# Revit family: Faucet_Kitchen-Two_Handle-American_Standard-Monterrey-6500.27X_Series
name_source: partatom
category: Plumbing Fixtures
units: mm (PartAtom-declared; Revit-internal decimal feet)

## family parameters
Always vertical = No
Cut with Voids When Loaded = No
OmniClass Number = 23.45.55.17
OmniClass Title = Mixing Faucets
Part Type = Normal
Room Calculation Point = No
Round Connector Dimension = Use Diameter
Shared = Yes
Work Plane-Based = Yes

## types (2) — shared parameters
ADA Compliant = Yes
ASME A112.18.1/CSA B125.1 = Yes
Assembly Code = D2020300
CW Connection = Yes
CWFU = 1.5
Cold Water Connection Diameter = 1/2"
Cold Water Connection Radius = 1/4"
Default Elevation = 0"
Description = Monterrey Two-Handle 8" Widespread Lavatory Faucet With Conventional Spout and Flexible Underbody.
Finish = Chrome-American_Standard-002-Polished
HW Connection = Yes
HWFU = 1.5
Height = 3 1/4"
Hot Water Connection Diameter = 1"
Hot Water Connection Radius = 1/4"
Installation Type = Deck Mounted
Length = 4 1/16"
Manufacturer = American Standard
Material = Chrome-American_Standard-002-Polished
Price = Prices may vary. Please consult Manufacturer Representative for most up-to-date price list.
Product Documentation Link = https://americanstandard.box.com
Product Page URL = https://www.americanstandard-us.com
URL = https://www.americanstandard-us.com
Vent Connection = No
WFU = 2
Waste Connection = No

## per-type parameters (varying)
| type | Flow Rate | Model |
| 6500.270.002 | 1.5 GPM | 6500.270 |
| 6500.275.002 | 0.5 GPM | 6500.275 |

## geometry (parser evidence)
native form markers: Sweep x2
no freeform markers — native parametric forms only
